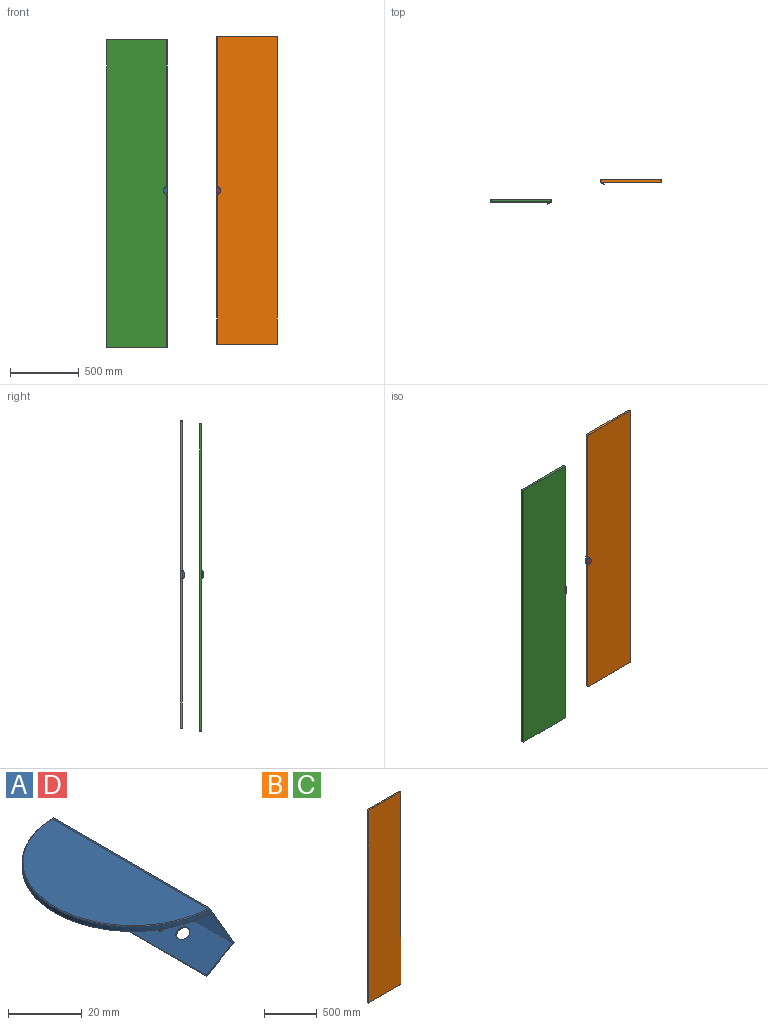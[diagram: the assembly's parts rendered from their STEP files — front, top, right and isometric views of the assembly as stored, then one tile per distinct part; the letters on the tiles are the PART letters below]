
ASSEMBLY  parts=4 mates=4
PART A: 26 faces, bbox 38.7x60x22 mm
  f0: plane 1.52x0.88mm, normal (0.87,0,0.5), area 0mm2, adj f2,f4,f17
  f1: plane 1.52x0.88mm, normal (0.87,0,0.5), area 0mm2, adj f2,f4,f19
  f2: cylinder r=30mm len=60mm, axis (0,0,-1), area 139.6mm2, adj f0,f1,f4,f5
  f3: plane 59.46x28.6mm, normal (0,0,1), area 1321.6mm2, adj f5,f15
  f4: cone r=30mm half-angle=45deg, axis (0,0,1), area 33.1mm2, adj f0,f1,f2,f6,f16
  f5: cone r=29.75mm half-angle=45deg, axis (0,0,-1), area 32.4mm2, adj f2,f3,f15
  f6: plane 59.5x29.75mm, normal (0,0,-1), area 945.2mm2, adj f4,f8,f9,f10,f16
  f7: plane 46x10mm, normal (0.5,0,-0.87), area 496.8mm2, adj f8,f9,f10,f12,f14,f16
  f8: plane 41.42x5.77mm, normal (-1,0,0), area 239.2mm2, adj f6,f7,f9,f10
  f9: cylinder r=23mm len=10mm, axis (0,0,1), area 30.4mm2, adj f6,f7,f8
  f10: cylinder r=23mm len=10mm, axis (0,0,1), area 30.4mm2, adj f6,f7,f8
  f11: cone r=0mm half-angle=59deg, axis (0.5,0,-0.87), area 10mm2, adj f12
  f12: cylinder r=1.65mm len=4.85mm, axis (0.5,0,-0.87), area 38.4mm2, adj f7,f11
  f13: cone r=0mm half-angle=59deg, axis (0.5,0,-0.87), area 10mm2, adj f14
  f14: cylinder r=1.65mm len=4.85mm, axis (0.5,0,-0.87), area 38.4mm2, adj f7,f13
  f15: plane 59.97x0.25mm, normal (0.87,0,0.5), area 17.2mm2, adj f3,f5,f18
  f16: plane 59.97x14.09mm, normal (-0.87,0,-0.5), area 959.5mm2, adj f4,f6,f7,f17,f19,f23
  f17: plane 22.04x10.64mm, normal (0,1,0), area 15mm2, adj f0,f16,f18,f20,f21,f22,f23
  f18: plane 59.97x0.43mm, normal (-0.5,0,0.87), area 30mm2, adj f15,f17,f19,f20
  f19: plane 22.04x10.64mm, normal (0,-1,0), area 15mm2, adj f1,f16,f18,f20,f21,f22,f23
  f20: plane 59.97x16.04mm, normal (0.87,0,0.5), area 1110.6mm2, adj f17,f18,f19,f22
  f21: plane 59.97x0.43mm, normal (-0.87,0,-0.5), area 30mm2, adj f17,f19,f22,f23
  f22: plane 59.97x10.39mm, normal (0.5,0,-0.87), area 694.5mm2, adj f17,f19,f20,f21,f24,f25
  f23: plane 59.97x9.96mm, normal (-0.5,0,0.87), area 664.5mm2, adj f16,f17,f19,f21,f24,f25
  f24: cylinder r=2mm len=4mm, axis (0.5,0,-0.87), area 6.3mm2, adj f22,f23
  f25: cylinder r=2mm len=4mm, axis (0.5,0,-0.87), area 6.3mm2, adj f22,f23
PART B: 18 faces, bbox 440.8x16x2240.8 mm
  f0: plane 430x15mm, normal (0,0,1), area 6450mm2, adj f5,f6,f9,f10
  f1: plane 2230x15mm, normal (-1,0,0), area 33450mm2, adj f5,f6,f7,f13
  f2: plane 430x15mm, normal (0,0,-1), area 6450mm2, adj f5,f7,f8,f17
  f3: plane 2230x15mm, normal (1,0,0), area 33450mm2, adj f5,f8,f9,f14
  f4: plane 2238x438mm, normal (0,-1,0), area 980230.3mm2, adj f10,f11,f12,f13,f14,f15,f16,f17
  f5: plane 2240x440mm, normal (0,1,0), area 985578.5mm2, adj f0,f1,f2,f3,f6,f7,f8,f9
  f6: cylinder r=5mm len=15mm, axis (0,-1,0), area 117.8mm2, adj f0,f1,f5,f11
  f7: cylinder r=5mm len=15mm, axis (0,1,0), area 117.8mm2, adj f1,f2,f5,f15
  f8: cylinder r=5mm len=15mm, axis (0,-1,0), area 117.8mm2, adj f2,f3,f5,f16
  f9: cylinder r=5mm len=15mm, axis (0,1,0), area 117.8mm2, adj f0,f3,f5,f12
  f10: cylinder r=1mm len=430mm, axis (1,0,0), area 675.4mm2, adj f0,f4,f11,f12
  f11: torus R=4mm, axis (0,-1,0), area 11.4mm2, adj f4,f6,f10,f13
  f12: torus R=4mm, axis (0,-1,0), area 11.4mm2, adj f4,f9,f10,f14
  f13: cylinder r=1mm len=2230mm, axis (0,0,1), area 3502.9mm2, adj f1,f4,f11,f15
  f14: cylinder r=1mm len=2230mm, axis (0,0,-1), area 3502.9mm2, adj f3,f4,f12,f16
  f15: torus R=4mm, axis (0,-1,0), area 11.4mm2, adj f4,f7,f13,f17
  f16: torus R=4mm, axis (0,-1,0), area 11.4mm2, adj f4,f8,f14,f17
  f17: cylinder r=1mm len=430mm, axis (-1,0,0), area 675.4mm2, adj f2,f4,f15,f16
PART C: same geometry as B
PART D: same geometry as A
PLACE A rot(axis=(0.94,0.25,0.25),93.8deg) t=(-542.17,200.3,599.13)mm
PLACE B t=(41.45,356.95,-206.12)mm
PLACE C t=(-760.68,216.3,-225.88)mm
PLACE D rot(axis=(-0.19,-0.69,0.69),158.9deg) t=(-180.04,341.45,599.13)mm
MATE parallel A.f7 <-> C.f4  axis (0,1,0) through (-547.87,200.3,599.13)mm
MATE parallel A.f17 <-> D.f19  axis (0,0,1) through (-544.22,210.99,629.11)mm
MATE fastened D.f16 <-> B.f1  axis (1,0,0) through (-180.04,349.45,599.13)mm
MATE parallel A.f16 <-> C.f3  axis (-1,0,0) through (-542.17,208.3,599.13)mm
